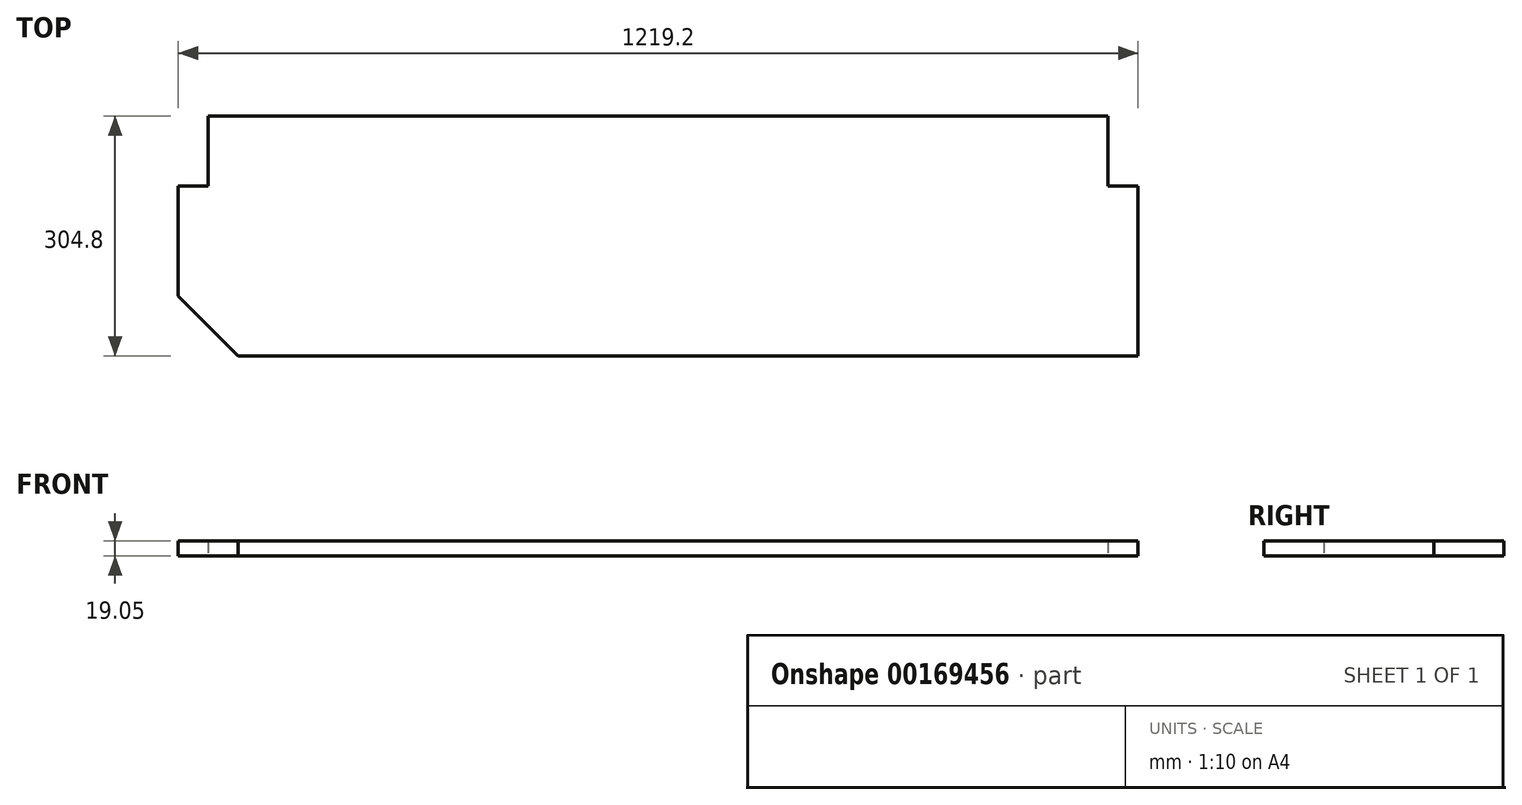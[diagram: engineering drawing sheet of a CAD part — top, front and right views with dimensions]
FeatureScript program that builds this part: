
annotation { "Feature Type Name" : "Feature", "Feature Type Description" : "" }
export const myFeature = defineFeature(function(context is Context, id is Id, definition is map)
    precondition{}
    {
        {
            var Q0;
            Q0=qCreatedBy(makeId("Top.planeOp"),FACE);
            var sketch = newSketch(context, id + "F0", { "sketchPlane" : qUnion([Q0])});
            skLineSegment(sketch, "E0", {"start": v(-134.12, 0) * mm, "end": v(1008.88, 0) * mm});
            skLineSegment(sketch, "E1", {"start": v(1046.98, -88.9) * mm, "end": v(1046.98, -304.8) * mm});
            skLineSegment(sketch, "E2", {"start": v(1046.98, -304.8) * mm, "end": v(-96, -304.8) * mm});
            skLineSegment(sketch, "E3", {"start": v(-96, -304.8) * mm, "end": v(-172.22, -228.6) * mm});
            skLineSegment(sketch, "E4", {"start": v(-172.22, -228.6) * mm, "end": v(-172.22, -88.9) * mm});
            skLineSegment(sketch, "E5", {"start": v(1008.88, 0) * mm, "end": v(1008.88, -88.9) * mm});
            skLineSegment(sketch, "E6", {"start": v(1008.88, -88.9) * mm, "end": v(1046.98, -88.9) * mm});
            skLineSegment(sketch, "E7", {"start": v(-172.22, -88.9) * mm, "end": v(-134.12, -88.9) * mm});
            skLineSegment(sketch, "E8", {"start": v(-134.12, -88.9) * mm, "end": v(-134.12, 0) * mm});
            skPoint(sketch, "E9.orphan", {"position": v(-172.22, 0) * mm});
            skSolve(sketch);
        }
        {
            var Q0;
            Q0 = qSketchRegion(id + "F0", true);
            extrude(context, id + "F1", {"entities" : qUnion([Q0]), "depth" : 19.05 * mm});
        }
    });
